# Revit family: Elevator_RES_NationwideLifts_Freedom-Hydro
name_source: partatom
category: Generic Models
units: mm (PartAtom-declared; Revit-internal decimal feet)

## family parameters
Always vertical = No
Can host rebar = No
Classification Number = 23.50.05.11.14.17
Cut with Voids When Loaded = No
Maintain Annotation Orientation = No
Part Type = Normal
Room Calculation Point = No
Round Connector Dimension = Use Diameter
Shared = No
Work Plane-Based = Yes

## types (1)
- Elevator_RES_NationwideLifts_Freedom-Hydro
    Assembly Code = D1010100
    Cab Design = Cab_Type1L
    Cab Style 2 Sliding Panel = Yes
    Cab Style Accordian Gate = No
    Center of Door A = 2' - 11"
    Center of Door B = 0' - 0"
    Center of Rail = 2' - 4"
    Default Elevation = 0' - 0"
    Expected Lifespan (Years) = 0
    Keynote = 14 20 00
    Lift Height = 0' - 0"
    Maintenance Schedule (Months) = 0
    Manufacturer = Nationwide Lifts, Inc.
    Manufacturer Website = http://www.elevators.com
    Model = As Specified
    Opening Depth = 4' - 8"
    Opening Width = 4' - 4"
    Product Data = http://www.arcat.com
    Revision = R1_2016-05
    Sales Information = http://www.elevators.com
    Space Between Cab and Hoistway = 0' - 0 3/4"
    Specification = http://www.arcat.com
    URL = http://www.elevators.com
    Unit Depth = 4' - 0"
    Unit Width = 3' - 0"
    Warranty Duration (Years) = 0

## geometry (parser evidence)
native form markers: Sweep x33
no freeform markers — native parametric forms only
